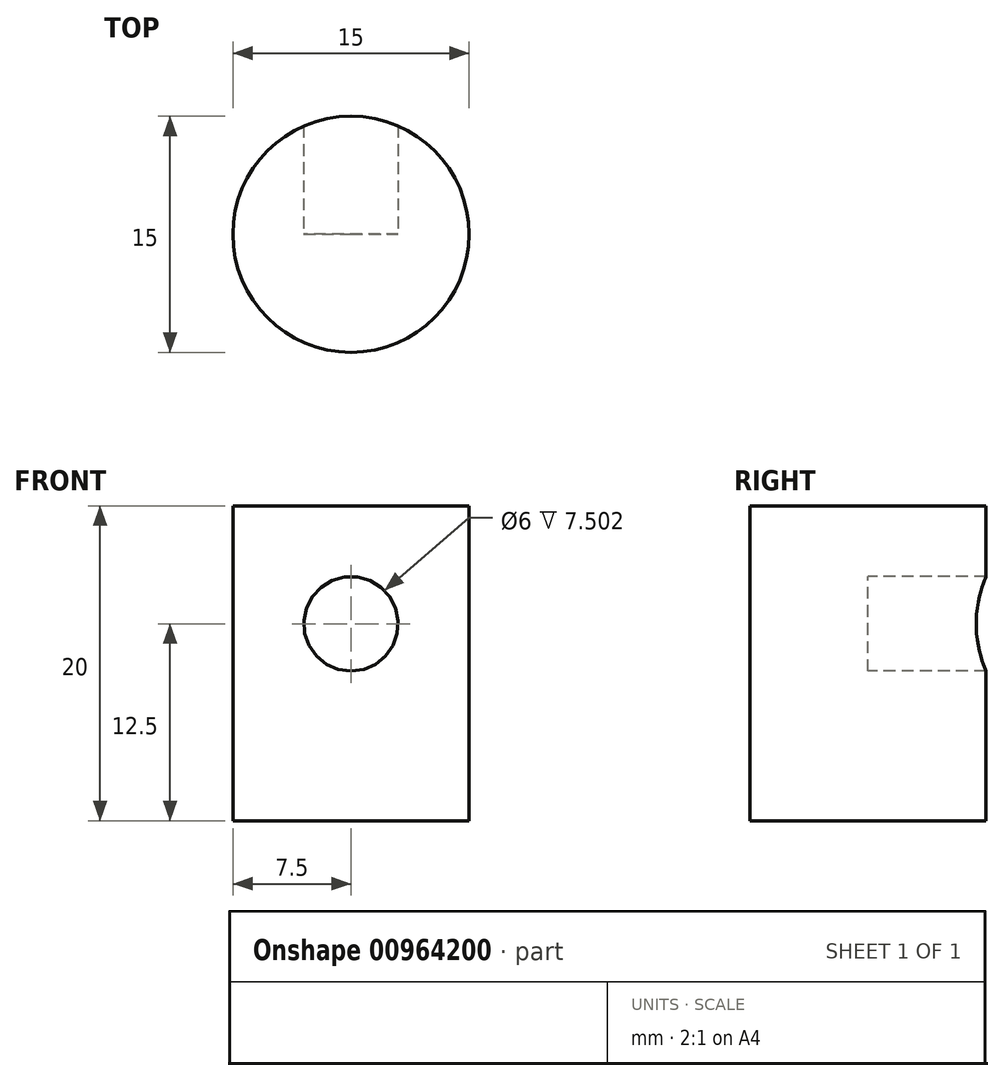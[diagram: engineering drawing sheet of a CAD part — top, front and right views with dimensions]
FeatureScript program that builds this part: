
annotation { "Feature Type Name" : "Feature", "Feature Type Description" : "" }
export const myFeature = defineFeature(function(context is Context, id is Id, definition is map)
    precondition{}
    {
        {
            var Q0;
            Q0=qCreatedBy(makeId("Top.planeOp"),FACE);
            var sketch = newSketch(context, id + "F0", { "sketchPlane" : qUnion([Q0])});
            skCircle(sketch, "E0", {"center": v(0, 0) * mm, "radius": 7.5 * mm});
            skSolve(sketch);
        }
        {
            var Q0;
            Q0=makeQuery(id+"F0.imprint","IMPRINT",FACE,{"disambiguationData":[TD([[makeQuery(id+"F0.imprint","IMPRINT",EDGE,{"derivedFrom":sQuery(id+"F0.wireOp",EDGE,"E0")}),1.0]])]});
            var Q1;
            Q1=sQuery(id+"F0.wireOp",EDGE,"E0");
            extrude(context, id + "F1", {"entities" : qUnion([Q0]), "surfaceEntities" : qUnion([Q1]), "depth" : 20 * mm, "offsetDistance" : 25 * mm});
        }
        {
            var Q0;
            Q0=qCreatedBy(makeId("Front.planeOp"),FACE);
            var sketch = newSketch(context, id + "F2", { "sketchPlane" : qUnion([Q0])});
            skCircle(sketch, "E1", {"center": v(0, 12.5) * mm, "radius": 3 * mm});
            skSolve(sketch);
        }
        {
            var Q0;
            Q0=qSketchRegion(id+"F2",true);
            extrude(context, id + "F3", {"entities" : qUnion([Q0]), "operationType" : NewBodyOperationType.REMOVE, "oppositeDirection" : true, "depth" : 25 * mm, "offsetDistance" : 25 * mm});
        }
    });
